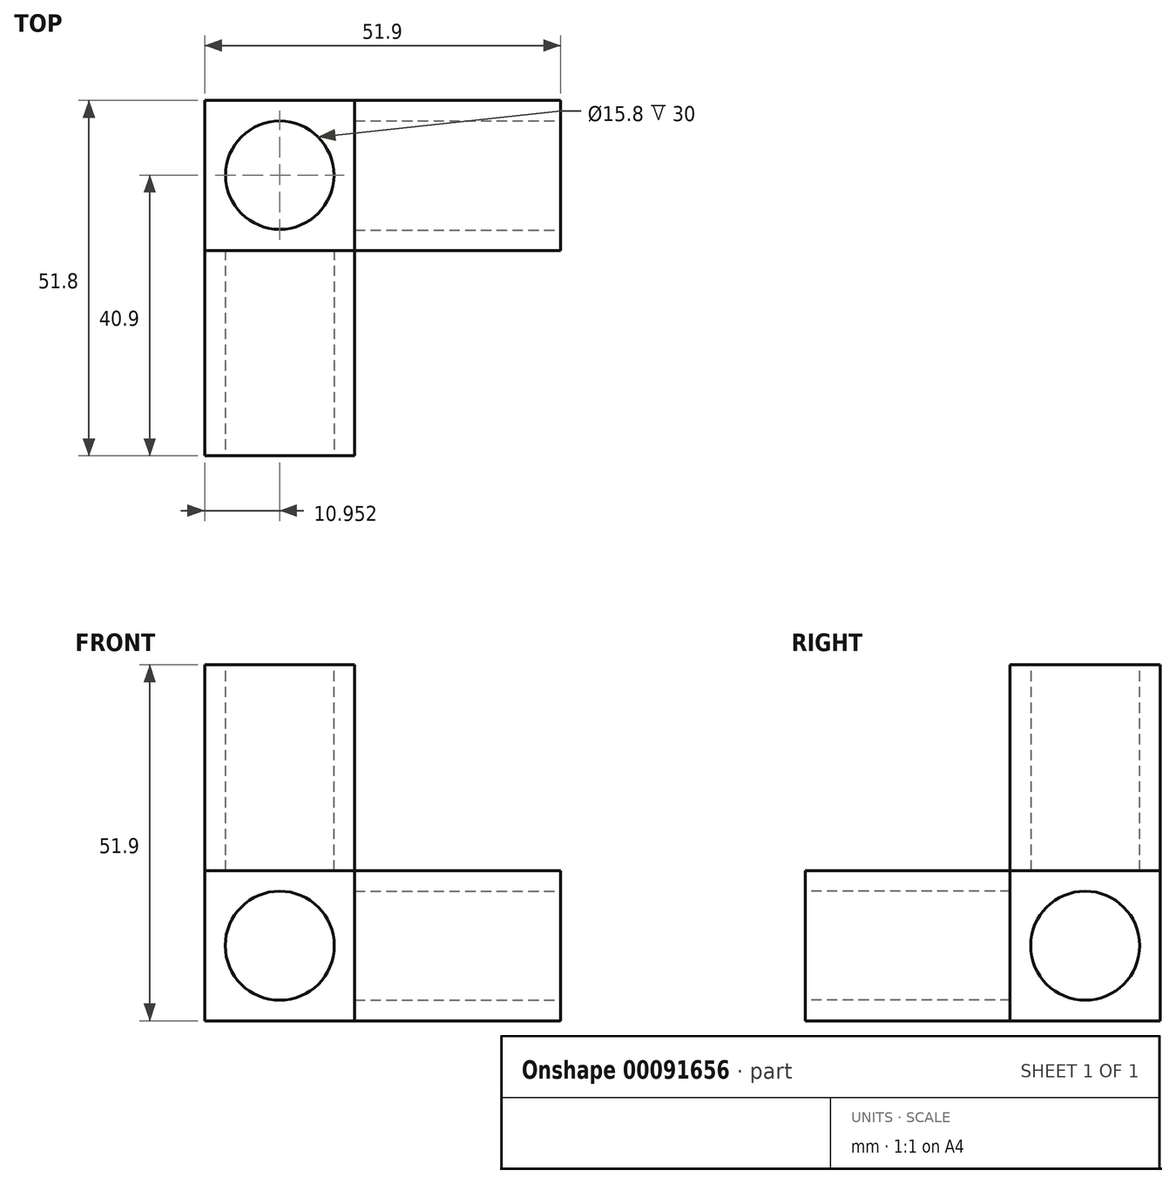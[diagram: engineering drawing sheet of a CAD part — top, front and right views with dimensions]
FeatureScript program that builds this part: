
annotation { "Feature Type Name" : "Feature", "Feature Type Description" : "" }
export const myFeature = defineFeature(function(context is Context, id is Id, definition is map)
    precondition{}
    {
        {
            var Q0;
            Q0=qCreatedBy(makeId("Front.planeOp"),FACE);
            var sketch = newSketch(context, id + "F0", { "sketchPlane" : qUnion([Q0])});
            skLineSegment(sketch, "E0.bottom", {"start": v(-42.3, 45.9) * mm, "end": v(-26.4, 45.9) * mm});
            skLineSegment(sketch, "E0.top", {"start": v(-42.3, 0) * mm, "end": v(-26.4, 0) * mm});
            skLineSegment(sketch, "E0.left", {"start": v(-42.3, 45.9) * mm, "end": v(-42.3, 0) * mm});
            skLineSegment(sketch, "E0.right", {"start": v(-26.4, 45.9) * mm, "end": v(-26.4, 15.9) * mm});
            skLineSegment(sketch, "E1.top", {"start": v(-42.3, 15.9) * mm, "end": v(-26.4, 15.9) * mm});
            skLineSegment(sketch, "E1.left", {"start": v(-42.3, 0) * mm, "end": v(-42.3, 15.9) * mm});
            skLineSegment(sketch, "E1.right", {"start": v(3.6, 0) * mm, "end": v(3.6, 15.9) * mm});
            skLineSegment(sketch, "E2", {"start": v(-26.4, 15.9) * mm, "end": v(-26.4, 0) * mm});
            skLineSegment(sketch, "E3", {"start": v(-26.4, 15.9) * mm, "end": v(3.6, 15.9) * mm});
            skLineSegment(sketch, "E4", {"start": v(-26.4, 0) * mm, "end": v(-26.4, 0) * mm});
            skLineSegment(sketch, "E5", {"start": v(-42.3, 15.9) * mm, "end": v(-42.3, 15.9) * mm});
            skLineSegment(sketch, "E6", {"start": v(-26.4, 0) * mm, "end": v(3.6, 0) * mm});
            skLineSegment(sketch, "E7.0", {"start": v(-45.3, 48.9) * mm, "end": v(-45.3, -3) * mm});
            skLineSegment(sketch, "E7.1", {"start": v(-45.3, -3) * mm, "end": v(-23.4, -3) * mm});
            skLineSegment(sketch, "E7.2", {"start": v(-23.4, 48.9) * mm, "end": v(-23.4, 18.9) * mm});
            skLineSegment(sketch, "E7.3", {"start": v(-23.4, 18.9) * mm, "end": v(6.6, 18.9) * mm});
            skLineSegment(sketch, "E7.4", {"start": v(6.6, -3) * mm, "end": v(6.6, 18.9) * mm});
            skLineSegment(sketch, "E7.5", {"start": v(-45.3, 48.9) * mm, "end": v(-23.4, 48.9) * mm});
            skLineSegment(sketch, "E7.6", {"start": v(-23.4, -3) * mm, "end": v(6.6, -3) * mm});
            skPoint(sketch, "E8", {"position": v(-34.36, 7.95) * mm});
            skPoint(sketch, "E8.positionSnap0", {"position": v(-26.4, 7.95) * mm});
            skPoint(sketch, "E8.positionSnap1", {"position": v(-34.36, 15.9) * mm});
            skCircle(sketch, "E9", {"center": v(-34.36, 7.95) * mm, "radius": 7.95 * mm});
            skLineSegment(sketch, "E10", {"start": v(-23.4, 18.9) * mm, "end": v(-45.3, 18.9) * mm});
            skLineSegment(sketch, "E11", {"start": v(-23.4, 18.9) * mm, "end": v(-23.4, -3) * mm});
            skSolve(sketch);
        }
        {
            var Q0;
            {var subQ1=sQuery(id+"F0.wireOp",EDGE,"E1.top");var subQ3=sQuery(id+"F0.wireOp",EDGE,"E9");var subQ4=makeQuery(id+"F0.imprint","INTERSECT",VERTEX,{"derivedFrom":[subQ1,subQ3]});Q0=makeQuery(id+"F0.imprint","IMPRINT",FACE,{"disambiguationData":[TD([[makeQuery(id+"F0.imprint","IMPRINT",EDGE,{"disambiguationData":[TD([[subQ4,-1.0]])],"derivedFrom":subQ3}),-1.0]])]});}
            var Q1;
            {var subQ0=sQuery(id+"F0.wireOp",EDGE,"E9");var subQ1=makeQuery(id+"F0.imprint","INTERSECT",VERTEX,{"derivedFrom":[sQuery(id+"F0.wireOp",EDGE,"E1.top"),subQ0]});Q1=makeQuery(id+"F0.imprint","IMPRINT",FACE,{"disambiguationData":[TD([[makeQuery(id+"F0.imprint","IMPRINT",EDGE,{"disambiguationData":[TD([[subQ1,1.0]])],"derivedFrom":subQ0}),1.0]])]});}
            var Q2;
            {var subQ5=sQuery(id+"F0.wireOp",EDGE,"E0.bottom");Q2=makeQuery(id+"F0.imprint","IMPRINT",FACE,{"disambiguationData":[TD([[makeQuery(id+"F0.imprint","IMPRINT",EDGE,{"derivedFrom":subQ5}),1.0]])]});}
            var Q3;
            {var subQ0=sQuery(id+"F0.wireOp",EDGE,"E1.right");Q3=makeQuery(id+"F0.imprint","IMPRINT",FACE,{"disambiguationData":[TD([[makeQuery(id+"F0.imprint","IMPRINT",EDGE,{"derivedFrom":subQ0}),1.0]])]});}
            var Q4;
            {var subQ0=sQuery(id+"F0.wireOp",EDGE,"E0.bottom");Q4=makeQuery(id+"F0.imprint","IMPRINT",FACE,{"disambiguationData":[TD([[makeQuery(id+"F0.imprint","IMPRINT",EDGE,{"derivedFrom":subQ0}),-1.0]])]});}
            var Q5;
            {var subQ0=sQuery(id+"F0.wireOp",EDGE,"E1.left");var subQ1=sQuery(id+"F0.wireOp",EDGE,"E0.top");var subQ2=makeQuery(id+"F0.imprint","INTERSECT",VERTEX,{"derivedFrom":[subQ1,subQ0]});Q5=makeQuery(id+"F0.imprint","IMPRINT",FACE,{"disambiguationData":[TD([[makeQuery(id+"F0.imprint","IMPRINT",EDGE,{"disambiguationData":[TD([[subQ2,-1.0]])],"derivedFrom":subQ1}),1.0]])]});}
            var Q6;
            {var subQ1=sQuery(id+"F0.wireOp",EDGE,"E0.top");var subQ3=sQuery(id+"F0.wireOp",EDGE,"E9");var subQ4=makeQuery(id+"F0.imprint","INTERSECT",VERTEX,{"derivedFrom":[subQ1,subQ3]});Q6=makeQuery(id+"F0.imprint","IMPRINT",FACE,{"disambiguationData":[TD([[makeQuery(id+"F0.imprint","IMPRINT",EDGE,{"disambiguationData":[TD([[subQ4,-1.0]])],"derivedFrom":subQ3}),-1.0]])]});}
            var Q7;
            {var subQ1=sQuery(id+"F0.wireOp",EDGE,"E1.top");var subQ3=sQuery(id+"F0.wireOp",EDGE,"E9");var subQ4=makeQuery(id+"F0.imprint","INTERSECT",VERTEX,{"derivedFrom":[subQ1,subQ3]});Q7=makeQuery(id+"F0.imprint","IMPRINT",FACE,{"disambiguationData":[TD([[makeQuery(id+"F0.imprint","IMPRINT",EDGE,{"disambiguationData":[TD([[subQ4,1.0]])],"derivedFrom":subQ3}),-1.0]])]});}
            var Q8;
            {var subQ5=sQuery(id+"F0.wireOp",EDGE,"E1.right");Q8=makeQuery(id+"F0.imprint","IMPRINT",FACE,{"disambiguationData":[TD([[makeQuery(id+"F0.imprint","IMPRINT",EDGE,{"derivedFrom":subQ5}),-1.0]])]});}
            var Q9;
            {var subQ4=sQuery(id+"F0.wireOp",EDGE,"E0.left");var subQ6=sQuery(id+"F0.wireOp",EDGE,"E10");var subQ8=makeQuery(id+"F0.imprint","INTERSECT",VERTEX,{"derivedFrom":[subQ4,subQ6]});Q9=makeQuery(id+"F0.imprint","IMPRINT",FACE,{"disambiguationData":[TD([[makeQuery(id+"F0.imprint","IMPRINT",EDGE,{"disambiguationData":[TD([[subQ8,1.0]])],"derivedFrom":subQ6}),1.0]])]});}
            var Q10;
            {var subQ3=sQuery(id+"F0.wireOp",EDGE,"E11");var subQ5=sQuery(id+"F0.wireOp",EDGE,"E3");var subQ8=makeQuery(id+"F0.imprint","INTERSECT",VERTEX,{"derivedFrom":[subQ5,subQ3]});Q10=makeQuery(id+"F0.imprint","IMPRINT",FACE,{"disambiguationData":[TD([[makeQuery(id+"F0.imprint","IMPRINT",EDGE,{"disambiguationData":[TD([[subQ8,-1.0]])],"derivedFrom":subQ3}),-1.0]])]});}
            var Q11;
            {var subQ14=sQuery(id+"F0.wireOp",EDGE,"E7.1");Q11=makeQuery(id+"F0.imprint","IMPRINT",FACE,{"disambiguationData":[TD([[makeQuery(id+"F0.imprint","IMPRINT",EDGE,{"derivedFrom":subQ14}),1.0]])]});}
            var Q12;
            {var subQ1=sQuery(id+"F0.wireOp",EDGE,"E0.right");var subQ3=sQuery(id+"F0.wireOp",EDGE,"E10");var subQ4=makeQuery(id+"F0.imprint","INTERSECT",VERTEX,{"derivedFrom":[subQ1,subQ3]});Q12=makeQuery(id+"F0.imprint","IMPRINT",FACE,{"disambiguationData":[TD([[makeQuery(id+"F0.imprint","IMPRINT",EDGE,{"disambiguationData":[TD([[subQ4,-1.0]])],"derivedFrom":subQ1}),1.0]])]});}
            extrude(context, id + "F1", {"entities" : qUnion([Q0, Q1, Q2, Q3, Q4, Q5, Q6, Q7, Q8, Q9, Q10, Q11, Q12]), "depth" : (15.9 + 6) * mm});
        }
        {
            var Q0;
            {var subQ14=sQuery(id+"F0.wireOp",EDGE,"E7.1");Q0=makeQuery(id+"F0.imprint","IMPRINT",FACE,{"disambiguationData":[TD([[makeQuery(id+"F0.imprint","IMPRINT",EDGE,{"derivedFrom":subQ14}),1.0]])]});}
            var Q1;
            {var subQ0=sQuery(id+"F0.wireOp",EDGE,"E9");var subQ1=makeQuery(id+"F0.imprint","INTERSECT",VERTEX,{"derivedFrom":[sQuery(id+"F0.wireOp",EDGE,"E1.top"),subQ0]});Q1=makeQuery(id+"F0.imprint","IMPRINT",FACE,{"disambiguationData":[TD([[makeQuery(id+"F0.imprint","IMPRINT",EDGE,{"disambiguationData":[TD([[subQ1,1.0]])],"derivedFrom":subQ0}),1.0]])]});}
            var Q2;
            {var subQ4=sQuery(id+"F0.wireOp",EDGE,"E0.left");var subQ6=sQuery(id+"F0.wireOp",EDGE,"E10");var subQ8=makeQuery(id+"F0.imprint","INTERSECT",VERTEX,{"derivedFrom":[subQ4,subQ6]});Q2=makeQuery(id+"F0.imprint","IMPRINT",FACE,{"disambiguationData":[TD([[makeQuery(id+"F0.imprint","IMPRINT",EDGE,{"disambiguationData":[TD([[subQ8,1.0]])],"derivedFrom":subQ6}),1.0]])]});}
            var Q3;
            {var subQ3=sQuery(id+"F0.wireOp",EDGE,"E11");var subQ5=sQuery(id+"F0.wireOp",EDGE,"E3");var subQ8=makeQuery(id+"F0.imprint","INTERSECT",VERTEX,{"derivedFrom":[subQ5,subQ3]});Q3=makeQuery(id+"F0.imprint","IMPRINT",FACE,{"disambiguationData":[TD([[makeQuery(id+"F0.imprint","IMPRINT",EDGE,{"disambiguationData":[TD([[subQ8,-1.0]])],"derivedFrom":subQ3}),-1.0]])]});}
            var Q4;
            {var subQ1=sQuery(id+"F0.wireOp",EDGE,"E0.right");var subQ3=sQuery(id+"F0.wireOp",EDGE,"E10");var subQ4=makeQuery(id+"F0.imprint","INTERSECT",VERTEX,{"derivedFrom":[subQ1,subQ3]});Q4=makeQuery(id+"F0.imprint","IMPRINT",FACE,{"disambiguationData":[TD([[makeQuery(id+"F0.imprint","IMPRINT",EDGE,{"disambiguationData":[TD([[subQ4,-1.0]])],"derivedFrom":subQ1}),1.0]])]});}
            var Q5;
            {var subQ1=sQuery(id+"F0.wireOp",EDGE,"E1.top");var subQ3=sQuery(id+"F0.wireOp",EDGE,"E9");var subQ4=makeQuery(id+"F0.imprint","INTERSECT",VERTEX,{"derivedFrom":[subQ1,subQ3]});Q5=makeQuery(id+"F0.imprint","IMPRINT",FACE,{"disambiguationData":[TD([[makeQuery(id+"F0.imprint","IMPRINT",EDGE,{"disambiguationData":[TD([[subQ4,1.0]])],"derivedFrom":subQ3}),-1.0]])]});}
            var Q6;
            {var subQ1=sQuery(id+"F0.wireOp",EDGE,"E1.top");var subQ3=sQuery(id+"F0.wireOp",EDGE,"E9");var subQ4=makeQuery(id+"F0.imprint","INTERSECT",VERTEX,{"derivedFrom":[subQ1,subQ3]});Q6=makeQuery(id+"F0.imprint","IMPRINT",FACE,{"disambiguationData":[TD([[makeQuery(id+"F0.imprint","IMPRINT",EDGE,{"disambiguationData":[TD([[subQ4,-1.0]])],"derivedFrom":subQ3}),-1.0]])]});}
            var Q7;
            {var subQ0=sQuery(id+"F0.wireOp",EDGE,"E1.left");var subQ1=sQuery(id+"F0.wireOp",EDGE,"E0.top");var subQ2=makeQuery(id+"F0.imprint","INTERSECT",VERTEX,{"derivedFrom":[subQ1,subQ0]});Q7=makeQuery(id+"F0.imprint","IMPRINT",FACE,{"disambiguationData":[TD([[makeQuery(id+"F0.imprint","IMPRINT",EDGE,{"disambiguationData":[TD([[subQ2,-1.0]])],"derivedFrom":subQ1}),1.0]])]});}
            var Q8;
            {var subQ1=sQuery(id+"F0.wireOp",EDGE,"E0.top");var subQ3=sQuery(id+"F0.wireOp",EDGE,"E9");var subQ4=makeQuery(id+"F0.imprint","INTERSECT",VERTEX,{"derivedFrom":[subQ1,subQ3]});Q8=makeQuery(id+"F0.imprint","IMPRINT",FACE,{"disambiguationData":[TD([[makeQuery(id+"F0.imprint","IMPRINT",EDGE,{"disambiguationData":[TD([[subQ4,-1.0]])],"derivedFrom":subQ3}),-1.0]])]});}
            extrude(context, id + "F2", {"entities" : qUnion([Q0, Q1, Q2, Q3, Q4, Q5, Q6, Q7, Q8]), "operationType" : NewBodyOperationType.ADD, "depth" : (15.8 + 6 + 30) * mm});
        }
        {
            var Q0;
            Q0=makeQuery(id+"F2.opExtrude","CAP_FACE",FACE,{"disambiguationData":[OSD([sQuery(id+"F0.wireOp",EDGE,"E7.0"),sQuery(id+"F0.wireOp",EDGE,"E7.1"),sQuery(id+"F0.wireOp",EDGE,"E10"),sQuery(id+"F0.wireOp",EDGE,"E11")])],"isStart":false});
            var sketch = newSketch(context, id + "F3", { "sketchPlane" : qUnion([Q0])});
            skCircle(sketch, "E12.0", {"center": v(-34.36, 7.95) * mm, "radius": 7.95 * mm});
            skSolve(sketch);
        }
        {
            var Q0;
            Q0=makeQuery(id+"F1.opExtrude","SWEPT_FACE",FACE,{"disambiguationData":[OSD([sQuery(id+"F0.wireOp",EDGE,"E7.5")])]});
            var sketch = newSketch(context, id + "F4", { "sketchPlane" : qUnion([Q0])});
            skPoint(sketch, "E13", {"position": v(-34.36, -3) * mm});
            skPoint(sketch, "E14", {"position": v(-26.4, -10.9) * mm});
            skPoint(sketch, "E15", {"position": v(-34.36, -10.9) * mm});
            skPoint(sketch, "E16", {"position": v(-62.98, 75) * mm});
            skPoint(sketch, "E17.orphan", {"position": v(-42.3, -3) * mm});
            skPoint(sketch, "E18.orphan", {"position": v(-26.4, -3) * mm});
            skPoint(sketch, "E19.orphan", {"position": v(-26.4, -18.8) * mm});
            skCircle(sketch, "E20", {"center": v(-34.36, -10.9) * mm, "radius": 7.9 * mm});
            skSolve(sketch);
        }
        {
            var Q0;
            Q0=makeQuery(id+"F1.opExtrude","SWEPT_FACE",FACE,{"disambiguationData":[OSD([sQuery(id+"F0.wireOp",EDGE,"E7.4")])]});
            var sketch = newSketch(context, id + "F5", { "sketchPlane" : qUnion([Q0])});
            skLineSegment(sketch, "E21.0", {"start": v(-18.9, 15.9) * mm, "end": v(-3, 15.9) * mm});
            skLineSegment(sketch, "E21.1", {"start": v(-18.9, 0) * mm, "end": v(-18.9, 15.9) * mm});
            skLineSegment(sketch, "E21.2", {"start": v(-18.9, 0) * mm, "end": v(-3, 0) * mm});
            skLineSegment(sketch, "E21.3", {"start": v(-3, 0) * mm, "end": v(-3, 15.9) * mm});
            skCircle(sketch, "E22", {"center": v(-10.95, 7.95) * mm, "radius": 7.95 * mm});
            skPoint(sketch, "E22.centerSnap0", {"position": v(-10.95, 0) * mm});
            skPoint(sketch, "E22.centerSnap1", {"position": v(-3, 7.95) * mm});
            skSolve(sketch);
        }
        {
            var Q0;
            Q0=makeQuery(id+"F3.imprint","IMPRINT",FACE,{"disambiguationData":[TD([[makeQuery(id+"F3.imprint","IMPRINT",EDGE,{"derivedFrom":sQuery(id+"F3.wireOp",EDGE,"E12.0")}),1.0]])]});
            extrude(context, id + "F6", {"entities" : qUnion([Q0]), "operationType" : NewBodyOperationType.REMOVE, "oppositeDirection" : true, "depth" : 30 * mm});
        }
        {
            var Q0;
            {var subQ0=sQuery(id+"F5.wireOp",EDGE,"E22");var subQ1=makeQuery(id+"F5.imprint","INTERSECT",VERTEX,{"derivedFrom":[sQuery(id+"F5.wireOp",EDGE,"E21.1"),subQ0]});Q0=makeQuery(id+"F5.imprint","IMPRINT",FACE,{"disambiguationData":[TD([[makeQuery(id+"F5.imprint","IMPRINT",EDGE,{"disambiguationData":[TD([[subQ1,1.0]])],"derivedFrom":subQ0}),1.0]])]});}
            extrude(context, id + "F7", {"entities" : qUnion([Q0]), "operationType" : NewBodyOperationType.REMOVE, "oppositeDirection" : true, "depth" : 30 * mm});
        }
        {
            var Q0;
            Q0=makeQuery(id+"F4.imprint","IMPRINT",FACE,{"disambiguationData":[TD([[makeQuery(id+"F4.imprint","IMPRINT",EDGE,{"derivedFrom":sQuery(id+"F4.wireOp",EDGE,"E20")}),1.0]])]});
            var Q1;
            Q1=sQuery(id+"F4.wireOp",EDGE,"E20");
            extrude(context, id + "F8", {"entities" : qUnion([Q0]), "operationType" : NewBodyOperationType.REMOVE, "surfaceEntities" : qUnion([Q1]), "oppositeDirection" : true, "depth" : 30 * mm});
        }
    });
